# Revit family: 1.Радиальный вентилятор для круглых каналов WNK
name_source: partatom
category: Оборудование
revit_build: Autodesk Revit 2016 (Build: 20151209_0715(x64)
units: mm (PartAtom-declared; Revit-internal decimal feet)

## family parameters
Всегда вертикально = Да
На основе рабочей плоскости = Нет
Общий = Нет
При загрузке вырезать с полостями = Нет
Размер круглого соединителя = Использовать диаметр
Тип детали = Нормальный
Точка расчета площади = Нет

## types (6) — shared parameters
Единица измерения = шт.
Завод изготовитель = KORF
Ключевая пометка = Вентиляция
Материал = Сталь серая
Наименование и тех.хар-ка = Радиальный вентилятор для круглых каналов
Напряжение U,В = 1-220
Отступ = 30 мм
Раздел = ОВ

## per-type parameters (varying)
| type | D | L | R | d | r | x | Масса единицы | Мощность двигателя N,Вт | Сила тока J, А | Тип, марка, обозначение | Частота вращения n, об/мин |
| 100/1 | 251 мм | 215 мм | 126 мм | 99 мм | 50 мм | 30 мм | 2.6 кг | 0.06 | 0.27 | WNK 100/1 | 2450 |
| 125/1 | 251 мм | 220 мм | 126 мм | 124 мм | 62 мм | 37 мм | 2.65 кг | 0.071 | 0.33 | WNK 125/1 | 2450 |
| 160/1 | 340 мм | 230 мм | 170 мм | 159 мм | 80 мм | 48 мм | 4 кг | 0.105 | 0.48 | WNK 160/1 | 2550 |
| 200/1 | 340 мм | 250 мм | 170 мм | 199 мм | 100 мм | 60 мм | 4.6 кг | 0.157 | 0.72 | WNK 200/1 | 2600 |
| 250/1 | 340 мм | 250 мм | 170 мм | 249 мм | 125 мм | 75 мм | 5 кг | 0.23 | 1.05 | WNK 250/1 | 2500 |
| 315/1 | 405 мм | 285 мм | 203 мм | 314 мм | 157 мм | 94 мм | 6.6 кг | 0.295 | 1.34 | WNK 315/1 | 2500 |
